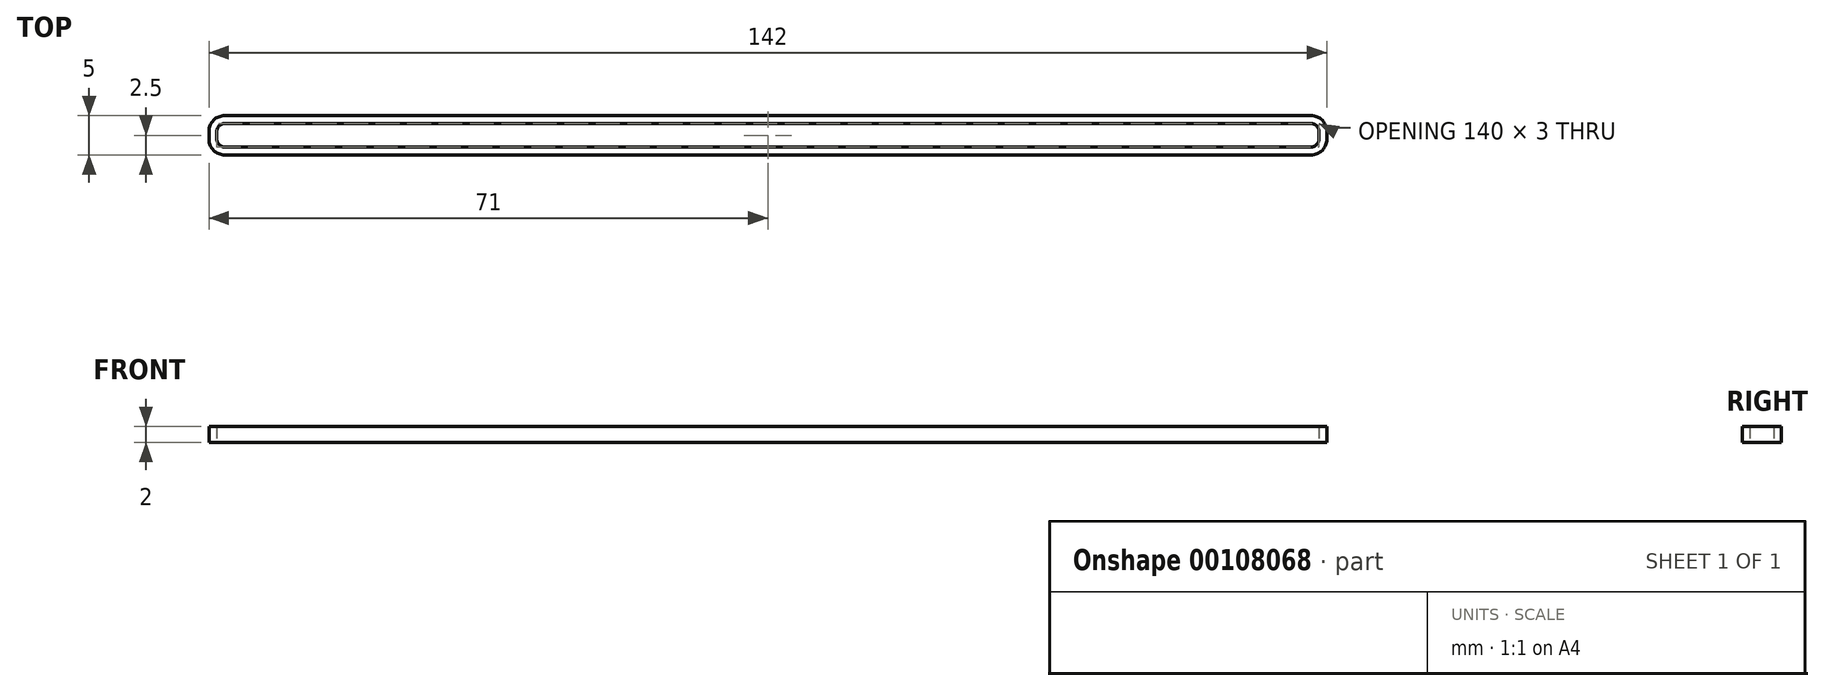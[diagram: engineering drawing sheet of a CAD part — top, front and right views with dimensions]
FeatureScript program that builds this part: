
annotation { "Feature Type Name" : "Feature", "Feature Type Description" : "" }
export const myFeature = defineFeature(function(context is Context, id is Id, definition is map)
    precondition{}
    {
        {
            var Q0;
            Q0=qCreatedBy(makeId("Top.planeOp"),FACE);
            var sketch = newSketch(context, id + "F0", { "sketchPlane" : qUnion([Q0])});
            skLineSegment(sketch, "E0.bottom", {"start": v(69, -1.5) * mm, "end": v(-69, -1.5) * mm});
            skLineSegment(sketch, "E0.top", {"start": v(69, 1.5) * mm, "end": v(-69, 1.5) * mm});
            skLineSegment(sketch, "E0.left", {"start": v(70, -0.5) * mm, "end": v(70, 0.5) * mm});
            skLineSegment(sketch, "E0.right", {"start": v(-70, -0.5) * mm, "end": v(-70, 0.5) * mm});
            skPoint(sketch, "E0.middle", {"position": v(0, 0) * mm});
            skPoint(sketch, "E1.visualSharp", {"position": v(-70, -1.5) * mm});
            skArc(sketch, "E1.filletArc", {"start": v(-70, -0.5) * mm, "mid": v(-69.7, -1.2) * mm, "end": v(-69, -1.5) * mm});
            skPoint(sketch, "E2.visualSharp", {"position": v(-70, 1.5) * mm});
            skArc(sketch, "E2.filletArc", {"start": v(-69, 1.5) * mm, "mid": v(-69.7, 1.2) * mm, "end": v(-70, 0.5) * mm});
            skPoint(sketch, "E3.visualSharp", {"position": v(70, 1.5) * mm});
            skArc(sketch, "E3.filletArc", {"start": v(70, 0.5) * mm, "mid": v(69.7, 1.2) * mm, "end": v(69, 1.5) * mm});
            skPoint(sketch, "E4.visualSharp", {"position": v(70, -1.5) * mm});
            skArc(sketch, "E4.filletArc", {"start": v(69, -1.5) * mm, "mid": v(69.7, -1.2) * mm, "end": v(70, -0.5) * mm});
            skArc(sketch, "E5.0", {"start": v(71, 0.5) * mm, "mid": v(70.41, 1.91) * mm, "end": v(69, 2.5) * mm});
            skLineSegment(sketch, "E5.1", {"start": v(71, -0.5) * mm, "end": v(71, 0.5) * mm});
            skLineSegment(sketch, "E5.2", {"start": v(69, 2.5) * mm, "end": v(-69, 2.5) * mm});
            skArc(sketch, "E5.3", {"start": v(69, -2.5) * mm, "mid": v(70.41, -1.91) * mm, "end": v(71, -0.5) * mm});
            skArc(sketch, "E5.4", {"start": v(-69, 2.5) * mm, "mid": v(-70.41, 1.91) * mm, "end": v(-71, 0.5) * mm});
            skLineSegment(sketch, "E5.5", {"start": v(-71, -0.5) * mm, "end": v(-71, 0.5) * mm});
            skArc(sketch, "E5.6", {"start": v(-71, -0.5) * mm, "mid": v(-70.41, -1.91) * mm, "end": v(-69, -2.5) * mm});
            skLineSegment(sketch, "E5.7", {"start": v(69, -2.5) * mm, "end": v(-69, -2.5) * mm});
            skSolve(sketch);
        }
        {
            var Q0;
            Q0=makeQuery(id+"F0.imprint","IMPRINT",FACE,{"disambiguationData":[TD([[makeQuery(id+"F0.imprint","IMPRINT",EDGE,{"derivedFrom":sQuery(id+"F0.wireOp",EDGE,"E0.bottom")}),1.0]])]});
            extrude(context, id + "F1", {"entities" : qUnion([Q0]), "depth" : 2 * mm});
        }
    });
